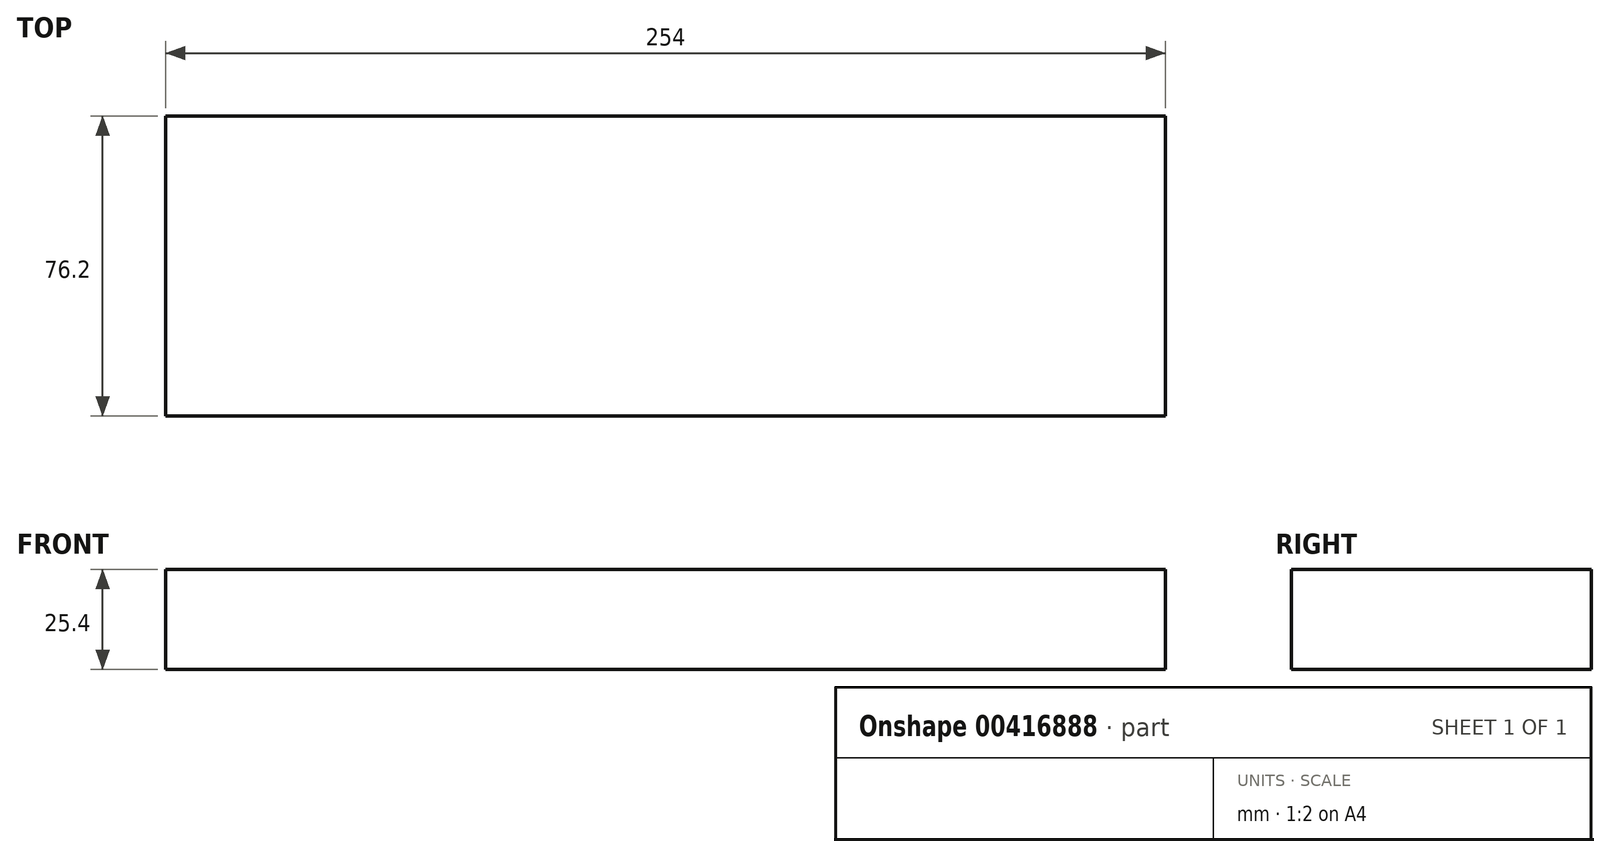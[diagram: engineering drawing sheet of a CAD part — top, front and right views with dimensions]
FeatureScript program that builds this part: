
annotation { "Feature Type Name" : "Feature", "Feature Type Description" : "" }
export const myFeature = defineFeature(function(context is Context, id is Id, definition is map)
    precondition{}
    {
        {
            var Q0;
            Q0=qCreatedBy(makeId("Top.planeOp"),FACE);
            var sketch = newSketch(context, id + "F0", { "sketchPlane" : qUnion([Q0])});
            skLineSegment(sketch, "E0.bottom", {"start": v(127, -38.1) * mm, "end": v(-127, -38.1) * mm});
            skLineSegment(sketch, "E0.top", {"start": v(127, 38.1) * mm, "end": v(-127, 38.1) * mm});
            skLineSegment(sketch, "E0.left", {"start": v(127, -38.1) * mm, "end": v(127, 38.1) * mm});
            skLineSegment(sketch, "E0.right", {"start": v(-127, -38.1) * mm, "end": v(-127, 38.1) * mm});
            skPoint(sketch, "E0.middle", {"position": v(0, 0) * mm});
            skSolve(sketch);
        }
        {
            var Q0;
            Q0=makeQuery(id+"F0.imprint","IMPRINT",FACE,{"disambiguationData":[TD([[makeQuery(id+"F0.imprint","IMPRINT",EDGE,{"derivedFrom":sQuery(id+"F0.wireOp",EDGE,"E0.bottom")}),-1.0]])]});
            extrude(context, id + "F1", {"entities" : qUnion([Q0]), "depth" : 25.4 * mm});
        }
    });
